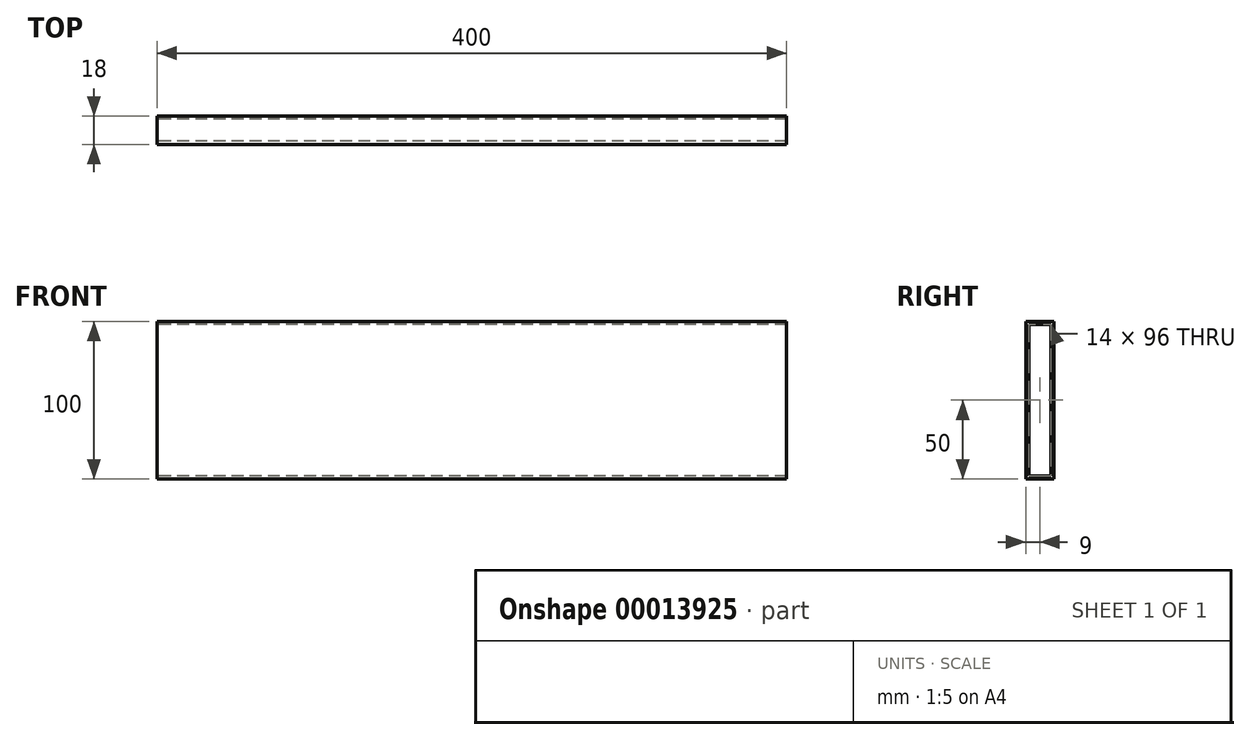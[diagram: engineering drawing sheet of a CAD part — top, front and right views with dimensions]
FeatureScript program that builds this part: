
annotation { "Feature Type Name" : "Feature", "Feature Type Description" : "" }
export const myFeature = defineFeature(function(context is Context, id is Id, definition is map)
    precondition{}
    {
        {
            var Q0;
            Q0=qCreatedBy(makeId("Right.planeOp"),FACE);
            var sketch = newSketch(context, id + "F0", { "sketchPlane" : qUnion([Q0])});
            skLineSegment(sketch, "E0.bottom", {"start": v(0, 0) * mm, "end": v(18, 0) * mm});
            skLineSegment(sketch, "E0.top", {"start": v(0, 100) * mm, "end": v(18, 100) * mm});
            skLineSegment(sketch, "E0.left", {"start": v(0, 0) * mm, "end": v(0, 100) * mm});
            skLineSegment(sketch, "E0.right", {"start": v(18, 0) * mm, "end": v(18, 100) * mm});
            skLineSegment(sketch, "E1.0", {"start": v(2, 98) * mm, "end": v(16, 98) * mm});
            skLineSegment(sketch, "E1.1", {"start": v(2, 2) * mm, "end": v(2, 98) * mm});
            skLineSegment(sketch, "E1.2", {"start": v(2, 2) * mm, "end": v(16, 2) * mm});
            skLineSegment(sketch, "E1.3", {"start": v(16, 2) * mm, "end": v(16, 98) * mm});
            skSolve(sketch);
        }
        {
            var Q0;
            Q0 = qSketchRegion(id + "F0", true);
            extrude(context, id + "F1", {"entities" : qUnion([Q0]), "depth" : 400 * mm});
        }
    });
